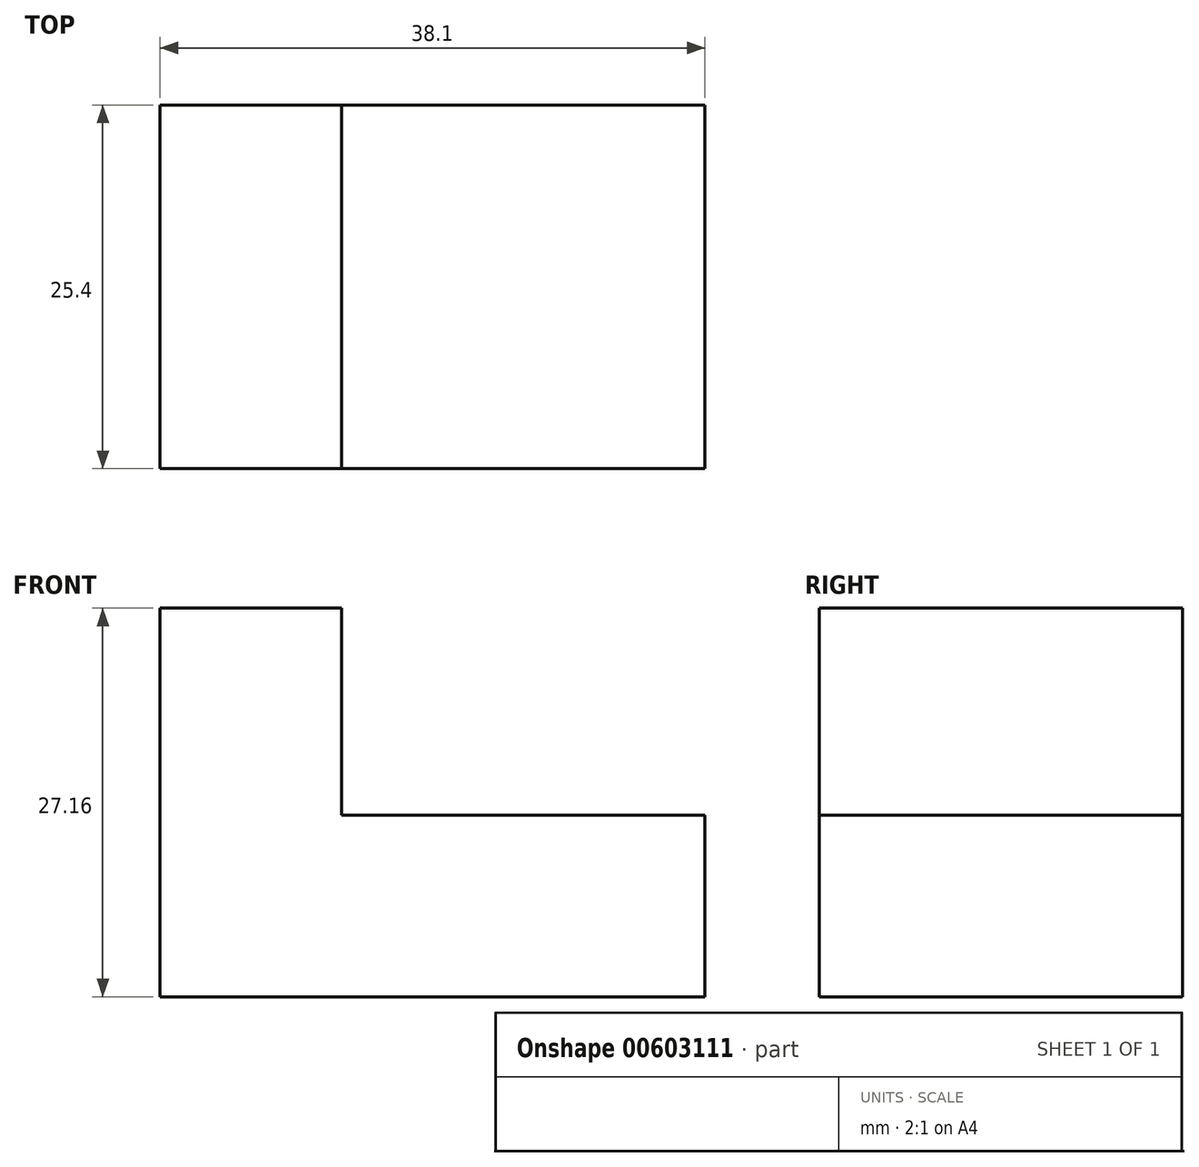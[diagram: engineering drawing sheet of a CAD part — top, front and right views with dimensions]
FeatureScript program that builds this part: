
annotation { "Feature Type Name" : "Feature", "Feature Type Description" : "" }
export const myFeature = defineFeature(function(context is Context, id is Id, definition is map)
    precondition{}
    {
        {
            var Q0;
            Q0=qCreatedBy(makeId("Front.planeOp"),FACE);
            var sketch = newSketch(context, id + "F0", { "sketchPlane" : qUnion([Q0])});
            skLineSegment(sketch, "E0", {"start": v(0, 0) * mm, "end": v(0, 27.16) * mm});
            skLineSegment(sketch, "E1", {"start": v(0, 27.16) * mm, "end": v(12.7, 27.16) * mm});
            skLineSegment(sketch, "E2", {"start": v(0, 0) * mm, "end": v(38.1, 0) * mm});
            skLineSegment(sketch, "E3", {"start": v(38.1, 0) * mm, "end": v(38.1, 12.7) * mm});
            skLineSegment(sketch, "E4", {"start": v(38.1, 12.7) * mm, "end": v(12.7, 12.7) * mm});
            skLineSegment(sketch, "E5", {"start": v(12.7, 27.16) * mm, "end": v(12.7, 12.7) * mm});
            skSolve(sketch);
        }
        {
            var Q0;
            Q0 = qSketchRegion(id + "F0", true);
            extrude(context, id + "F1", {"entities" : qUnion([Q0]), "depth" : 25.4 * mm, "offsetDistance" : 25.4 * mm});
        }
    });
